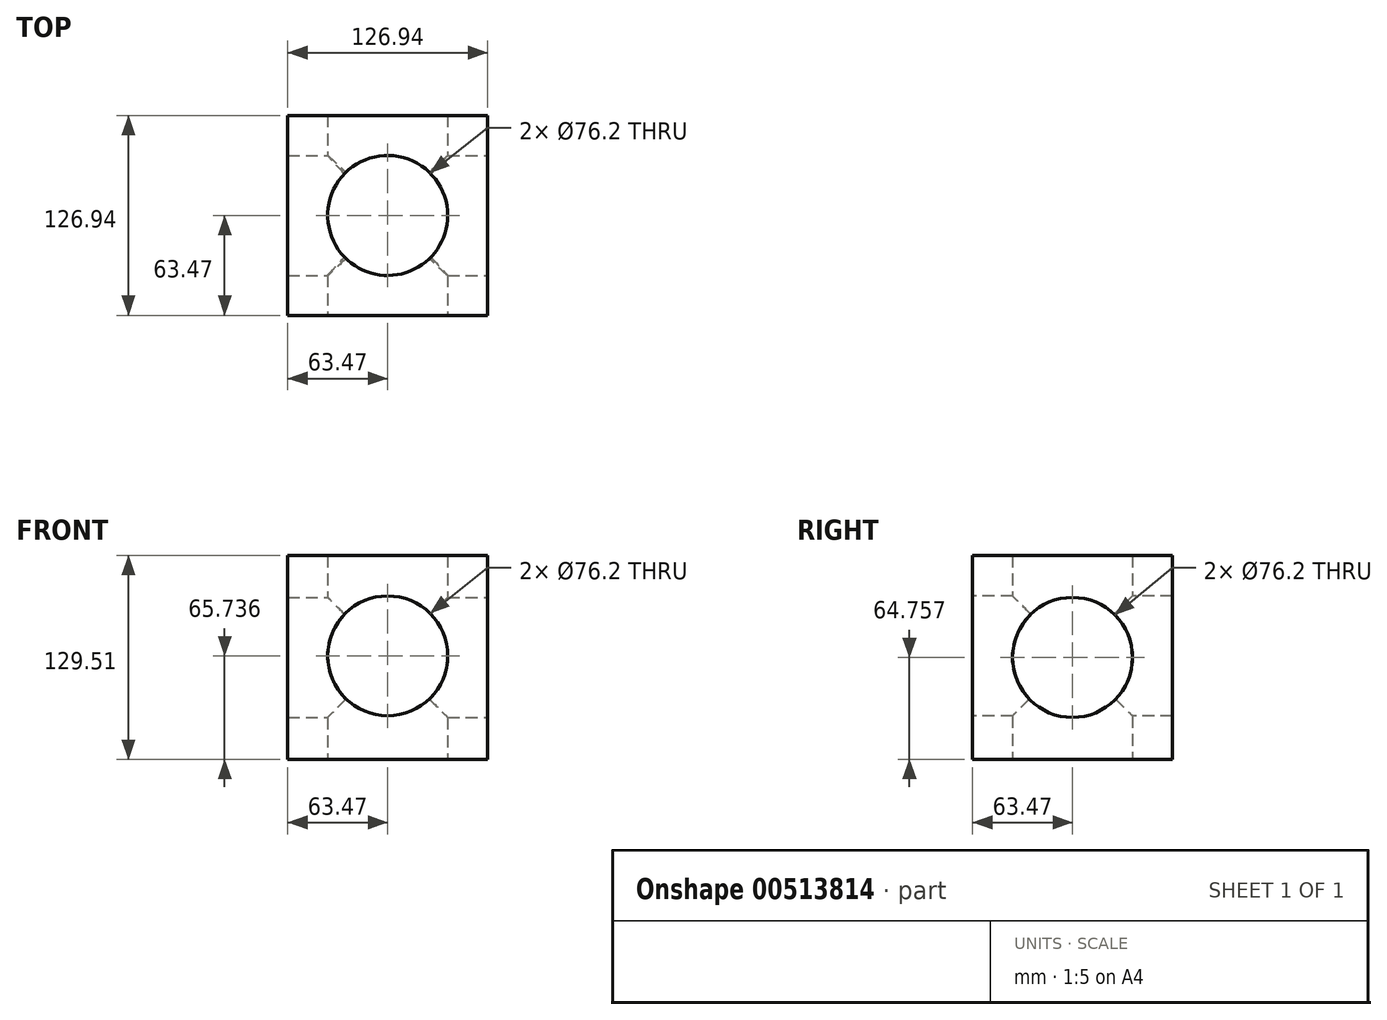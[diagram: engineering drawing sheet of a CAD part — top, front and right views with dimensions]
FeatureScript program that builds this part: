
annotation { "Feature Type Name" : "Feature", "Feature Type Description" : "" }
export const myFeature = defineFeature(function(context is Context, id is Id, definition is map)
    precondition{}
    {
        {
            var Q0;
            Q0=qCreatedBy(makeId("Top.planeOp"),FACE);
            var sketch = newSketch(context, id + "F0", { "sketchPlane" : qUnion([Q0])});
            skLineSegment(sketch, "E0.bottom", {"start": v(-63.47, 63.47) * mm, "end": v(63.47, 63.47) * mm});
            skLineSegment(sketch, "E0.top", {"start": v(-63.47, -63.47) * mm, "end": v(63.47, -63.47) * mm});
            skLineSegment(sketch, "E0.left", {"start": v(-63.47, 63.47) * mm, "end": v(-63.47, -63.47) * mm});
            skLineSegment(sketch, "E0.right", {"start": v(63.47, 63.47) * mm, "end": v(63.47, -63.47) * mm});
            skPoint(sketch, "E0.middle", {"position": v(0, 0) * mm});
            skCircle(sketch, "E1", {"center": v(0, 0) * mm, "radius": 38.1 * mm});
            skSolve(sketch);
        }
        {
            var Q0;
            Q0=makeQuery(id+"F0.imprint","IMPRINT",FACE,{"disambiguationData":[TD([[makeQuery(id+"F0.imprint","IMPRINT",EDGE,{"derivedFrom":sQuery(id+"F0.wireOp",EDGE,"E0.bottom")}),-1.0]])]});
            extrude(context, id + "F1", {"entities" : qUnion([Q0]), "depth" : 129.5 * mm});
        }
        {
            var Q0;
            Q0=makeQuery(id+"F1.opExtrude","SWEPT_FACE",FACE,{"disambiguationData":[OSD([sQuery(id+"F0.wireOp",EDGE,"E0.top")])]});
            var sketch = newSketch(context, id + "F2", { "sketchPlane" : qUnion([Q0])});
            skCircle(sketch, "E2", {"center": v(0, 65.74) * mm, "radius": 38.1 * mm});
            skPoint(sketch, "E2.centerSnap0", {"position": v(0, 0) * mm});
            skSolve(sketch);
        }
        {
            var Q0;
            Q0=makeQuery(id+"F2.imprint","IMPRINT",FACE,{"disambiguationData":[TD([[makeQuery(id+"F2.imprint","IMPRINT",EDGE,{"derivedFrom":sQuery(id+"F2.wireOp",EDGE,"E2")}),1.0]])]});
            extrude(context, id + "F3", {"entities" : qUnion([Q0]), "operationType" : NewBodyOperationType.REMOVE, "oppositeDirection" : true, "depth" : 129.5 * mm});
        }
        {
            var Q0;
            Q0=makeQuery(id+"F1.opExtrude","SWEPT_FACE",FACE,{"disambiguationData":[OSD([sQuery(id+"F0.wireOp",EDGE,"E0.right")])]});
            var sketch = newSketch(context, id + "F4", { "sketchPlane" : qUnion([Q0])});
            skCircle(sketch, "E3", {"center": v(0, 64.76) * mm, "radius": 38.1 * mm});
            skPoint(sketch, "E3.centerSnap0", {"position": v(0, 0) * mm});
            skSolve(sketch);
        }
        {
            var Q0;
            Q0=makeQuery(id+"F4.imprint","IMPRINT",FACE,{"disambiguationData":[TD([[makeQuery(id+"F4.imprint","IMPRINT",EDGE,{"derivedFrom":sQuery(id+"F4.wireOp",EDGE,"E3")}),1.0]])]});
            extrude(context, id + "F5", {"entities" : qUnion([Q0]), "operationType" : NewBodyOperationType.REMOVE, "oppositeDirection" : true, "depth" : 129.5 * mm});
        }
    });
